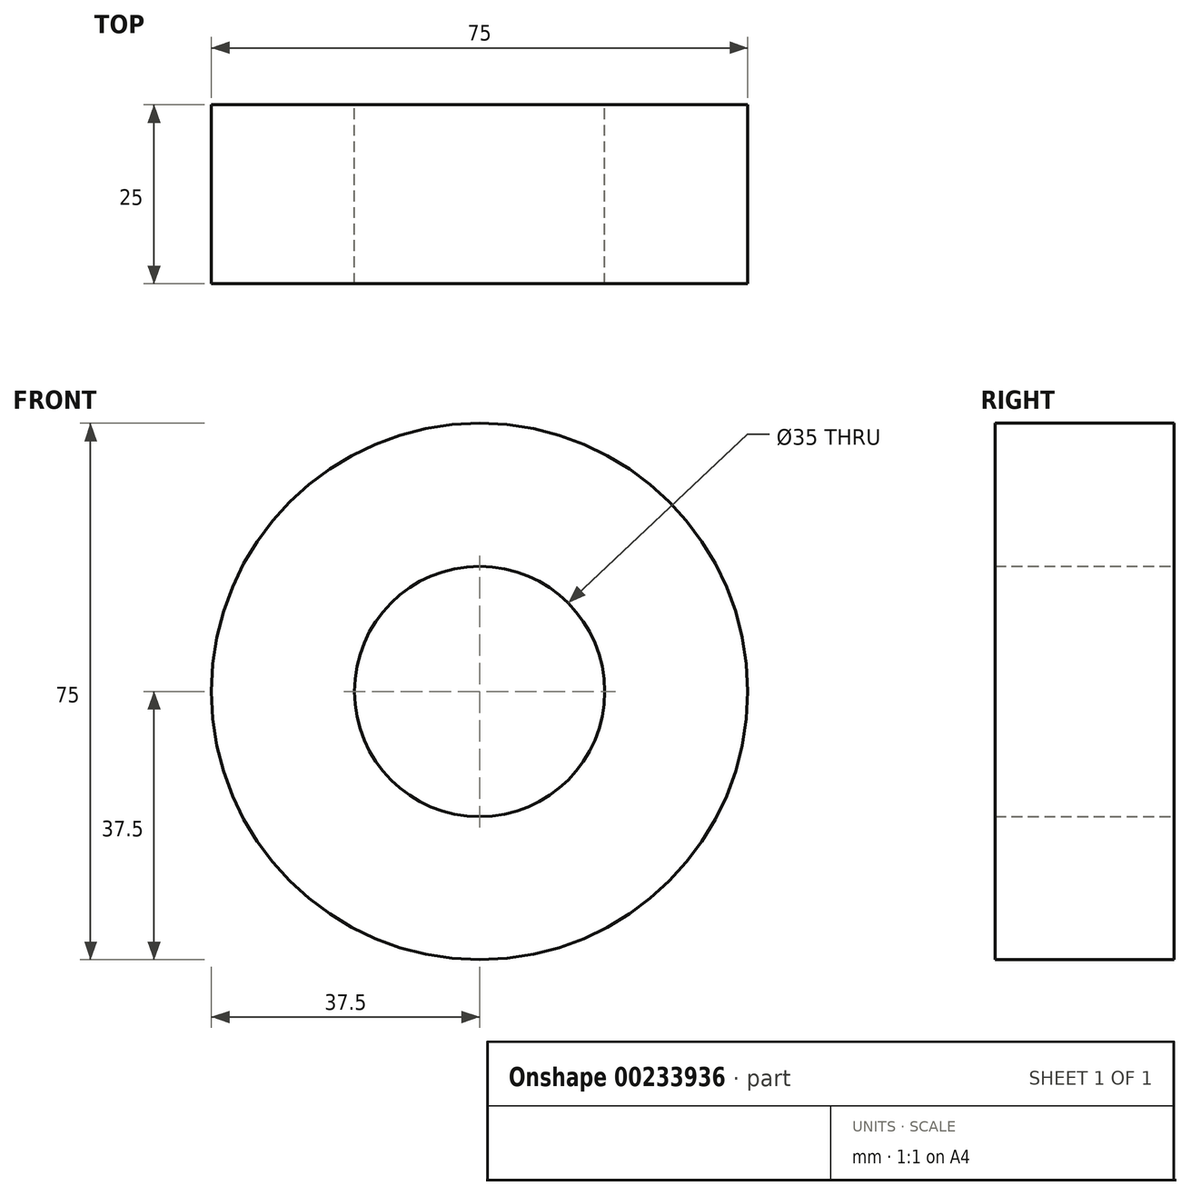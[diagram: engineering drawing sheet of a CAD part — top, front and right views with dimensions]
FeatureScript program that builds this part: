
annotation { "Feature Type Name" : "Feature", "Feature Type Description" : "" }
export const myFeature = defineFeature(function(context is Context, id is Id, definition is map)
    precondition{}
    {
        {
            var Q0;
            Q0=qCreatedBy(makeId("Front.planeOp"),FACE);
            var sketch = newSketch(context, id + "F2", { "sketchPlane" : qUnion([Q0])});
            skCircle(sketch, "E0", {"center": v(0, 0) * mm, "radius": 37.5 * mm});
            skCircle(sketch, "E1", {"center": v(0, 0) * mm, "radius": 17.5 * mm});
            skCircle(sketch, "E2", {"center": v(0, 0) * mm, "radius": 10 * mm});
            skSolve(sketch);
        }
        {
            var Q0;
            Q0 = qSketchRegion(id + "F2", true);
            extrude(context, id + "F0", {"entities" : qUnion([Q0]), "depth" : 25 * mm});
        }
    });
